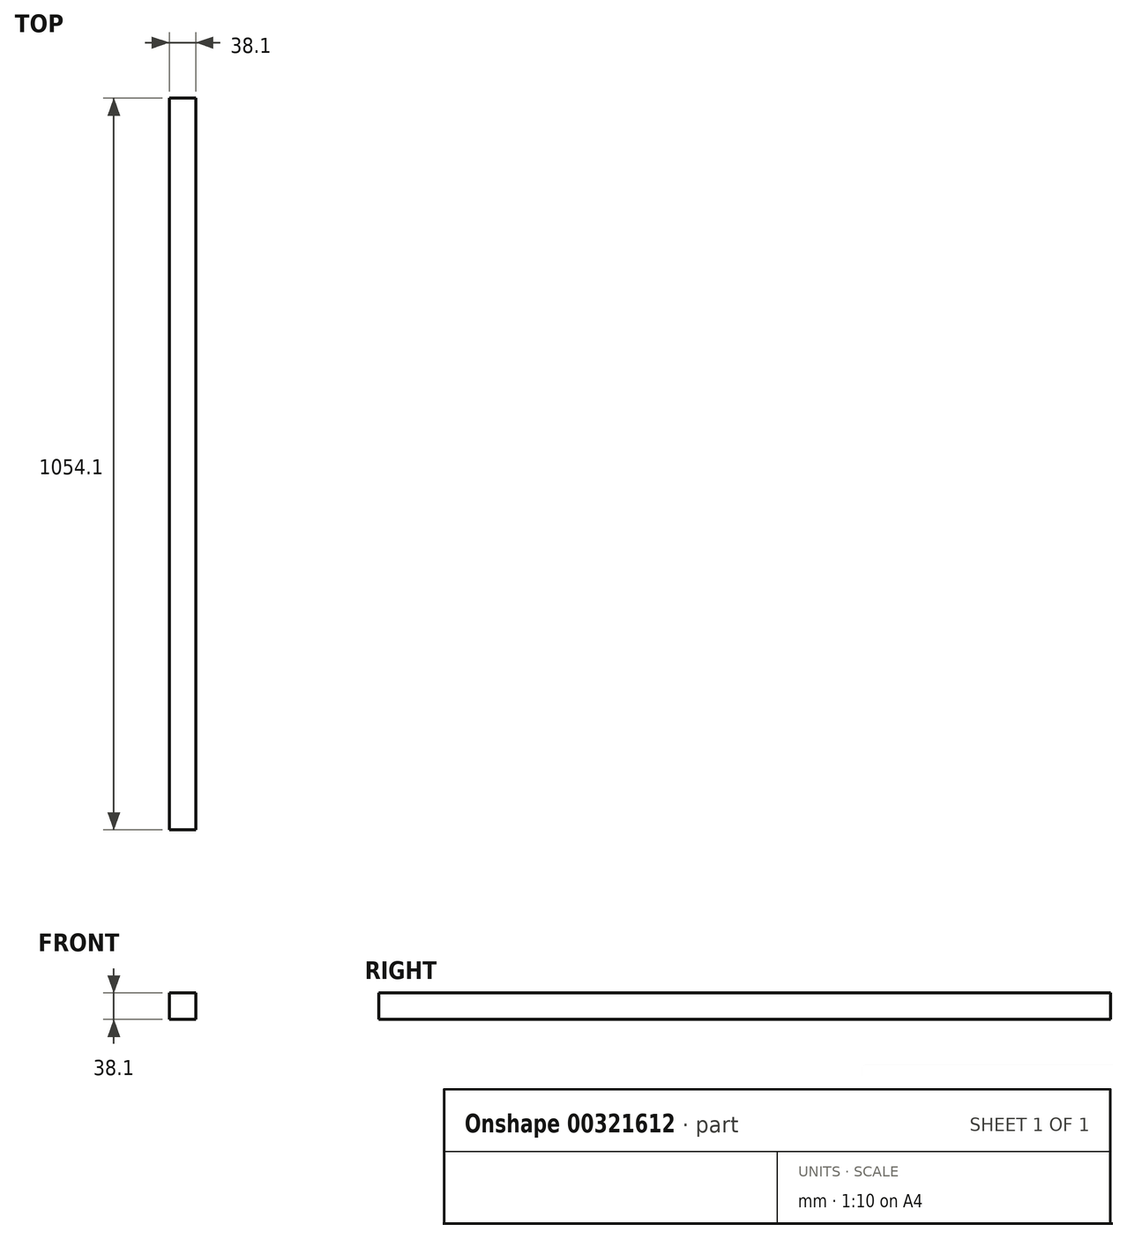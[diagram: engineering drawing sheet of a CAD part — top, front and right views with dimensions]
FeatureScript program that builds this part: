
annotation { "Feature Type Name" : "Feature", "Feature Type Description" : "" }
export const myFeature = defineFeature(function(context is Context, id is Id, definition is map)
    precondition{}
    {
        {
            var Q0;
            Q0=qCreatedBy(makeId("Front.planeOp"),FACE);
            var sketch = newSketch(context, id + "F0", { "sketchPlane" : qUnion([Q0])});
            skLineSegment(sketch, "E0.bottom", {"start": v(-32.38, 14.96) * mm, "end": v(5.72, 14.96) * mm});
            skLineSegment(sketch, "E0.top", {"start": v(-32.38, -23.14) * mm, "end": v(5.72, -23.14) * mm});
            skLineSegment(sketch, "E0.left", {"start": v(-32.38, 14.96) * mm, "end": v(-32.38, -23.14) * mm});
            skLineSegment(sketch, "E0.right", {"start": v(5.72, 14.96) * mm, "end": v(5.72, -23.14) * mm});
            skSolve(sketch);
        }
        {
            var Q0;
            Q0=makeQuery(id+"F0.imprint","IMPRINT",FACE,{"disambiguationData":[TD([[makeQuery(id+"F0.imprint","IMPRINT",EDGE,{"derivedFrom":sQuery(id+"F0.wireOp",EDGE,"E0.bottom")}),-1.0]])]});
            extrude(context, id + "F1", {"entities" : qUnion([Q0]), "depth" : 1054.1 * mm});
        }
    });
